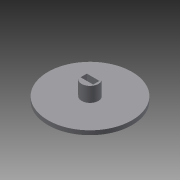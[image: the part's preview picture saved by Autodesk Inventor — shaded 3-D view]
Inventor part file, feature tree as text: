
AUTODESK INVENTOR PART (.ipt)
format: ipt  version: 2015 (Build 190159000, 159)  size: 88,576 bytes
history: native  units: mm
features: extrude x3, sketch x3
ambient origin geometry x8: Origin, YZ Plane, XZ Plane, XY Plane, X Axis, Y Axis, Z Axis, Center Point
bodies: Solid1 (feature_tree)
feature tree (6):
  extrude  "Extrusion1"  Depth=2.0mm TaperAngle=0.0deg
  extrude  "Extrusion2"  Depth=7.0mm TaperAngle=0.0deg
  extrude  "Extrusion3"  Depth=3.0mm
  sketch  "Sketch1"  dims[d0=40.0mm d1=2.0mm d2=0.0mm]
  sketch  "Sketch2"  dims[d3=8.0mm d4=7.0mm d5=0.0mm]
  sketch  "Sketch3"  dims[d6=6.0mm d7=3.0mm d8=1.5mm d9=3.0mm d10=3.0mm d11=7.0mm d12=0.0mm]
